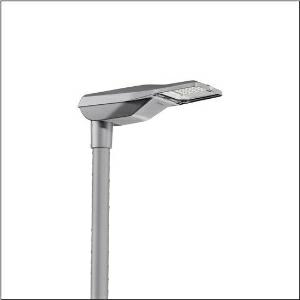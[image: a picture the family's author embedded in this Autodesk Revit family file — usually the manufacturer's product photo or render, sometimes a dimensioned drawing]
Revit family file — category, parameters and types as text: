
# Revit family: streetlight_sl_21_iq_micro___p0_8ab_5xe1r31g08db_e4e9
name_source: partatom
category: Lighting Fixtures
units: mm (PartAtom-declared; Revit-internal decimal feet)

## family parameters
Cut with Voids When Loaded = No
Host = Face
Light Source = No
Part Type = Normal
Room Calculation Point = No
Round Connector Dimension = Use Diameter
Shared = No

## types (1)
- --- (1 x LED, 4220 lm, 36.4 W, 3000K)
    Apparent Load = 36 VA
    CIE Flux Codes = 36 71 98 100 100
    Color Rendering = 70
    Color Temperature = 3000K
    Default Elevation = 1800 mm
    Description = Streetlight SL 21 iQ micro, mast luminaire, primary light control with lens, of PMMA, primary optical cover: cover, of toughened safety glass, transparent, light distribution: P0.8aB, light emission: direct distribution, primary light characteristic: asymmetric, installation type: post-top, side-entry, LED, High Power LED, rated luminous flux: 4.220lm, luminous efficacy: 116lm/W, light colour: 730, colour temperature: 3000K, control gear: iQ Street-Remote, control: pre-setting: linear dimming characteristic, Street-Remote, Auto-Match, Temp-Guard, Lumen-Switch, Night-Set, Smart-Wire, Light-Fading, Desk-Remote (wireless, voltage-free reading and setting of iQ features in the workshop via application-optimized NFC function/RFID function), optimised constant luminous flux control (CLO 2.0), mains connection: 220..240V, AC, 50/60Hz, start of lifetime: 36W, end of service life: 38W, reduction: 16W, luminaire housing, of diecast aluminium, powder-coated, Siteco® metallic grey (DB 702S), corrosivity category C5 mid according to DIN EN ISO 12944, please order mast flange separately, inclination adjustable: 0°, 5°, 10°, 15°, sealing non-destructively replaceable, multi-level sealing system, length: 528mm, width: 235mm, height: 110mm, mast flange for spigot size: 42mm (side-entry): 5XC10008XM4, 60/48mm (side-entry/post-top): 5XC10108XM2, 76/60mm (side-entry/post-top): 5XC10108XM1, protection rating (complete): IP66, insulation class (complete): insulation class II (safety insulation), certification: CE, ENEC, ENEC+, VDE, impact resistance: IK09, permissible operating ambient temperature for outdoor applications: -40..+50°C, standard-compliant lighting for roads and squares, packaging unit: 1 piece

Light Distribution: P0.8aB
    Height = 110 mm
    Lamp = 1 x LED
    Lamp Light Flux = 4220 lm
    Lamp Power = 36.4 W
    Lamp count = 1
    Length = 528 mm
    Luminous efficacy = 116 lm/W
    Manufacturer = Siteco
    ModVariant = No
    Model = 5XE1R31G08DB
    Number of Poles = 1
    OnlyDefault = Yes
    Power Factor = 1
    Product Name = Streetlight SL 21 iQ micro | P0.8aB
    Product group = mast luminaire | pylon top
    ProductGroupID = 6100
    Protection Class = Protection class II
    Protection Degree = IP 66
    RLX_Detail_Level = 1
    RLX_Emergency_Light_Flux = 0 lm
    RLX_Emergency_Type = 0
    RLX_Emergency_Type_DB = No
    RlxData = <blob elided: 98381 chars, md5=ab15c8fc>
    Socket = socket
    Standby Power = 0 W
    System Light Flux = 4220 lm
    System Power = 36 W
    Type Comments = factory setting: luminous flux: 100 % | dim-lin: 254 | 715 mA
    Type Image = l_1006881.jpg
    URL = http://relux.com
    VarID = @adj_071828
    Voltage = 0 V
    Weight = 0.00 kg
    Width = 235 mm

## geometry (parser evidence)
native form markers: Blend x4, Sweep x10
no freeform markers — native parametric forms only
